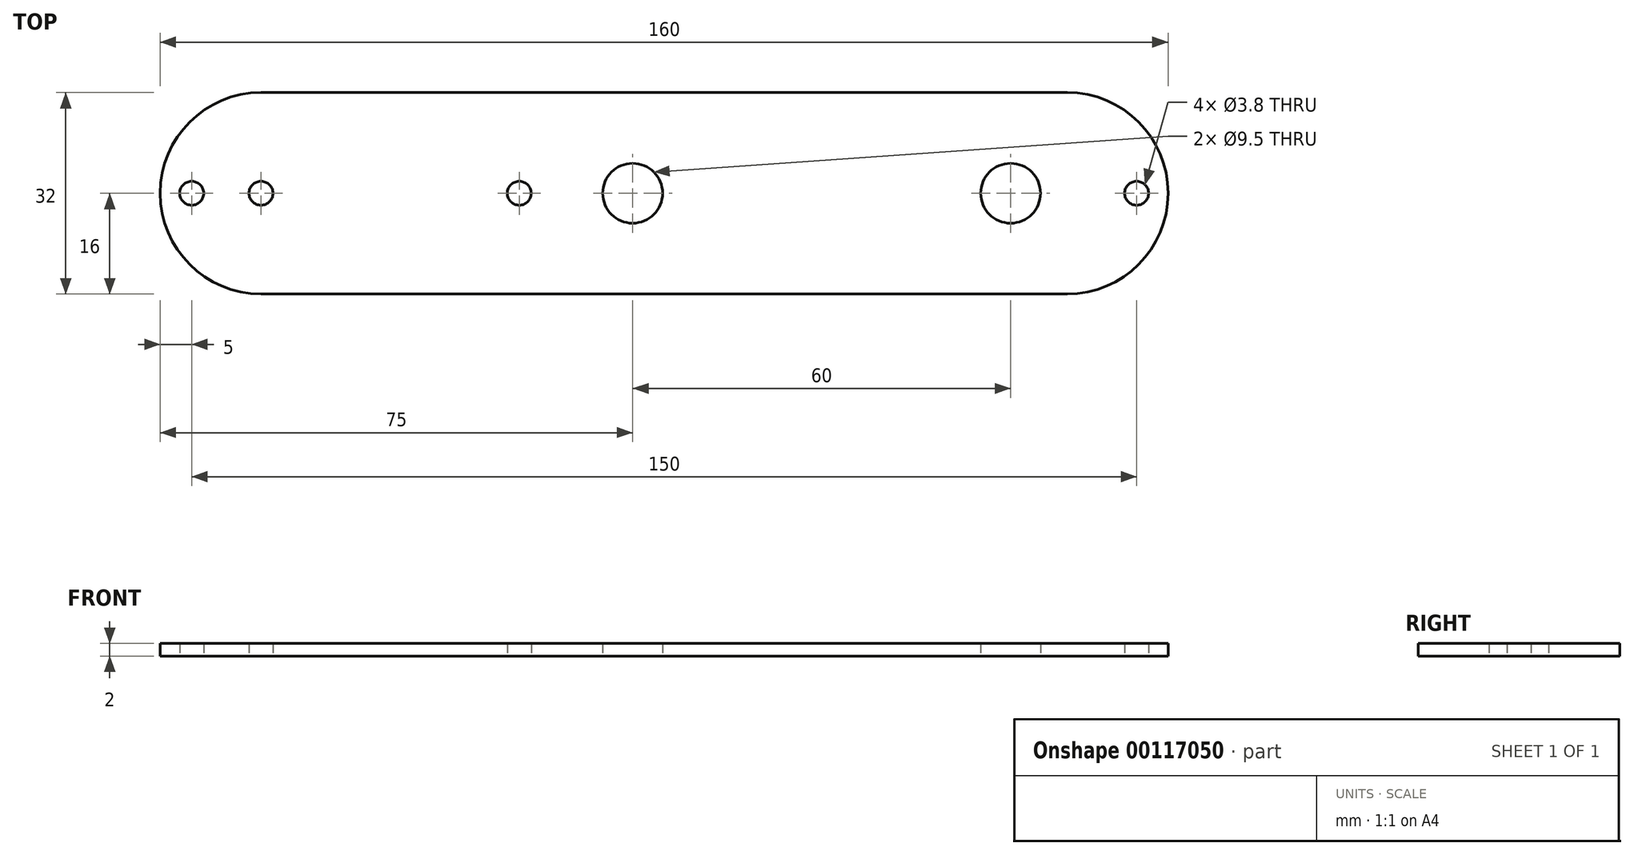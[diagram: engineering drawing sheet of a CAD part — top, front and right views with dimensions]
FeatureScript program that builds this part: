
annotation { "Feature Type Name" : "Feature", "Feature Type Description" : "" }
export const myFeature = defineFeature(function(context is Context, id is Id, definition is map)
    precondition{}
    {
        {
            var Q0;
            Q0=qCreatedBy(makeId("Top.planeOp"),FACE);
            var sketch = newSketch(context, id + "F0", { "sketchPlane" : qUnion([Q0])});
            skArc(sketch, "E0", {"start": v(0, 16) * mm, "mid": v(-16, 0) * mm, "end": v(0, -16) * mm});
            skLineSegment(sketch, "E1", {"start": v(-16, 0) * mm, "end": v(144, 0) * mm, "construction": true});
            skArc(sketch, "E2", {"start": v(128, -16) * mm, "mid": v(144, 0) * mm, "end": v(128, 16) * mm});
            skLineSegment(sketch, "E3", {"start": v(0, 16) * mm, "end": v(128, 16) * mm});
            skLineSegment(sketch, "E4", {"start": v(0, -16) * mm, "end": v(128, -16) * mm});
            skCircle(sketch, "E5", {"center": v(-11, 0) * mm, "radius": 1.9 * mm});
            skCircle(sketch, "E6", {"center": v(139, 0) * mm, "radius": 1.9 * mm});
            skCircle(sketch, "E7", {"center": v(0, 0) * mm, "radius": 1.9 * mm});
            skCircle(sketch, "E8", {"center": v(41, 0) * mm, "radius": 1.9 * mm});
            skCircle(sketch, "E9", {"center": v(59, 0) * mm, "radius": 4.75 * mm});
            skCircle(sketch, "E10", {"center": v(119, 0) * mm, "radius": 4.75 * mm});
            skSolve(sketch);
        }
        {
            var Q0;
            Q0=makeQuery(id+"F0.imprint","IMPRINT",FACE,{"disambiguationData":[TD([[makeQuery(id+"F0.imprint","IMPRINT",EDGE,{"derivedFrom":sQuery(id+"F0.wireOp",EDGE,"E0")}),1.0]])]});
            extrude(context, id + "F1", {"entities" : qUnion([Q0]), "depth" : 2 * mm});
        }
    });
